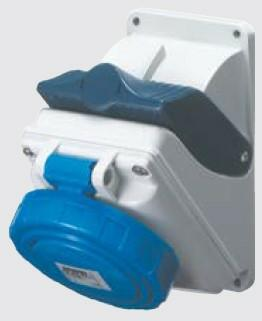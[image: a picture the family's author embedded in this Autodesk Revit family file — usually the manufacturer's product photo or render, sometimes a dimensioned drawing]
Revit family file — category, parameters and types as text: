
# Revit family: Building-IEC309Connections-GEWISS-COMBIBLOC-INTERLOCKED-SOCKET-OUTLETS_IP55_WITHOUT_BOTTOM
name_source: partatom
category: Apparecchi elettrici
units: mm (PartAtom-declared; Revit-internal decimal feet)

## family parameters
Condiviso = No
Host = Superficie
Mantenere orientamento annotazione = Sì
Punto di calcolo locali = Sì
Quota connettore circolare = Usa diametro
Taglio con vuoti quando caricato = No
Tipo di parte = Normale

## types (18) — shared parameters
BLOCCO = B=C
Catalogue = BUILDING
Electrocod = 2221
FORMULA = 1000 mm  [stored 3.28084 ft]
Frequency = 50/60 Hz
Glow wire test: = 850 °C (active parts) - 650 °C (passive parts)
IDF = 4224a358-be41-4ae5-826c-8098fafd2300
IDT = 73411960965b40fc900c2c175d51bdd6
IP degree = IP55
Immagine tipo = COMBIBLOC55.jpg
L = 155 mm
N.poli = 1
Operating temperature: = -25 +40 °C
POMELLO = bianco
PRESA = Giallo
Produttore = GEWISS S.p.A.
Prospetto di default = 1219 mm
Protection = NO (SBF)
SEO = Interlocked outlet
STRUTTURA = RAL - 7035
STRUTTURA ALTA = blue
Shock resistance = IK08
Spostamento_S = 1500 mm
Technical sheet = https://www.gewiss.com
Thermo-pressure with ball = 125
Typology = Compact
URL = https://www.gewiss.com
VETRO = Vetro
Version file RFA = 21.4
Voltaggio = 0 V
W = 115 mm
With back-mounting box = No

## per-type parameters (varying)
| type | Colour: | Descrizione | Modello | No. of poles | Rated current (A) | Rated voltage | Reference h |
| GW66467 - COMBIBLOC N.B.IP55 2P+E 16A 110V 4H | Yellow | COMBIBLOC N.B.IP55 2P+E 16A 110V 4H | GW66467 | 2P+E | 16 | 100-130V | 4 |
| GW66486 - COMBIBLOC N.B.IP55 3P+N+E 32A 400V 6H | Red | COMBIBLOC N.B.IP55 3P+N+E 32A 400V 6H | GW66486 | 3P+N+E | 32 | 380-415V | 6 |
| GW66474 - COMBIBLOC N.B.IP55 3P+E 16A 400V 6H | Red | COMBIBLOC N.B.IP55 3P+E 16A 400V 6H | GW66474 | 3P+E | 16 | 380-415V | 6 |
| GW66469 - COMBIBLOC N.B.IP55 3P+N+E 16A 110V 4H | Yellow | COMBIBLOC N.B.IP55 3P+N+E 16A 110V 4H | GW66469 | 3P+N+E | 16 | 100-130V | 4 |
| GW66482 - COMBIBLOC N.B.IP55 3P+E 32A 230V 9H | Blue | COMBIBLOC N.B.IP55 3P+E 32A 230V 9H | GW66482 | 3P+E | 32 | 200-250V | 9 |
| GW66472 - COMBIBLOC N.B.IP55 3P+N+E 16A 230V 9H | Blue | COMBIBLOC N.B.IP55 3P+N+E 16A 230V 9H | GW66472 | 3P+N+E | 16 | 200-250V | 9 |
| GW66478 - COMBIBLOC N.B.IP55 2P+E 32A 110V 4H | Yellow | COMBIBLOC N.B.IP55 2P+E 32A 110V 4H | GW66478 | 2P+E | 32 | 100-130V | 4 |
| GW66468 - COMBIBLOC N.B.IP55 3P+E 16A 110V 4H | Yellow | COMBIBLOC N.B.IP55 3P+E 16A 110V 4H | GW66468 | 3P+E | 16 | 100-130V | 4 |
| GW66475 - COMBIBLOC N.B.IP55 3P+N+E 16A 400V 6H | Red | COMBIBLOC N.B.IP55 3P+N+E 16A 400V 6H | GW66475 | 3P+N+E | 16 | 380-415V | 6 |
| GW66484 - COMBIBLOC N.B.IP55 2P+E 32A 400V 9H | Red | COMBIBLOC N.B.IP55 2P+E 32A 400V 9H | GW66484 | 2P+E | 32 | 380-415V | 9 |
| GW66485 - COMBIBLOC N.B.IP55 3P+E 32A 400V 6H | Red | COMBIBLOC N.B.IP55 3P+E 32A 400V 6H | GW66485 | 3P+E | 32 | 380-415V | 6 |
| GW66481 - COMBIBLOC N.B.IP55 2P+E 32A 230V 6H | Blue | COMBIBLOC N.B.IP55 2P+E 32A 230V 6H | GW66481 | 2P+E | 32 | 200-250V | 6 |
| GW66483 - COMBIBLOC N.B.IP55 3P+N+E 32A 230V 9H | Blue | COMBIBLOC N.B.IP55 3P+N+E 32A 230V 9H | GW66483 | 3P+N+E | 32 | 200-250V | 9 |
| GW66480 - COMBIBLOC N.B.IP55 3P+N+E 32A 110V 4H | Yellow | COMBIBLOC N.B.IP55 3P+N+E 32A 110V 4H | GW66480 | 3P+N+E | 32 | 100-130V | 4 |
| GW66473 - COMBIBLOC N.B.IP55 2P+E 16A 400V 9H | Red | COMBIBLOC N.B.IP55 2P+E 16A 400V 9H | GW66473 | 2P+E | 16 | 380-415V | 9 |
| GW66471 - COMBIBLOC N.B.IP55 3P+E 16A 230V 9H | Blue | COMBIBLOC N.B.IP55 3P+E 16A 230V 9H | GW66471 | 3P+E | 16 | 200-250V | 9 |
| GW66479 - COMBIBLOC N.B.IP55 3P+E 32A 110V 4H | Yellow | COMBIBLOC N.B.IP55 3P+E 32A 110V 4H | GW66479 | 3P+E | 32 | 100-130V | 4 |
| GW66470 - COMBIBLOC N.B.IP55 2P+E 16A 230V 6H | Blue | COMBIBLOC N.B.IP55 2P+E 16A 230V 6H | GW66470 | 2P+E | 16 | 200-250V | 6 |

note: source unit labels omitted for Thermo-pressure with ball — the stored unit's dimension contradicts the parameter name (converter mislabeling)

note: [stored X ft] marks values corroborated as IEEE doubles in the binary element streams (Revit-internal decimal feet)

## geometry (parser evidence)
native form markers: Sweep x3
no freeform markers — native parametric forms only
